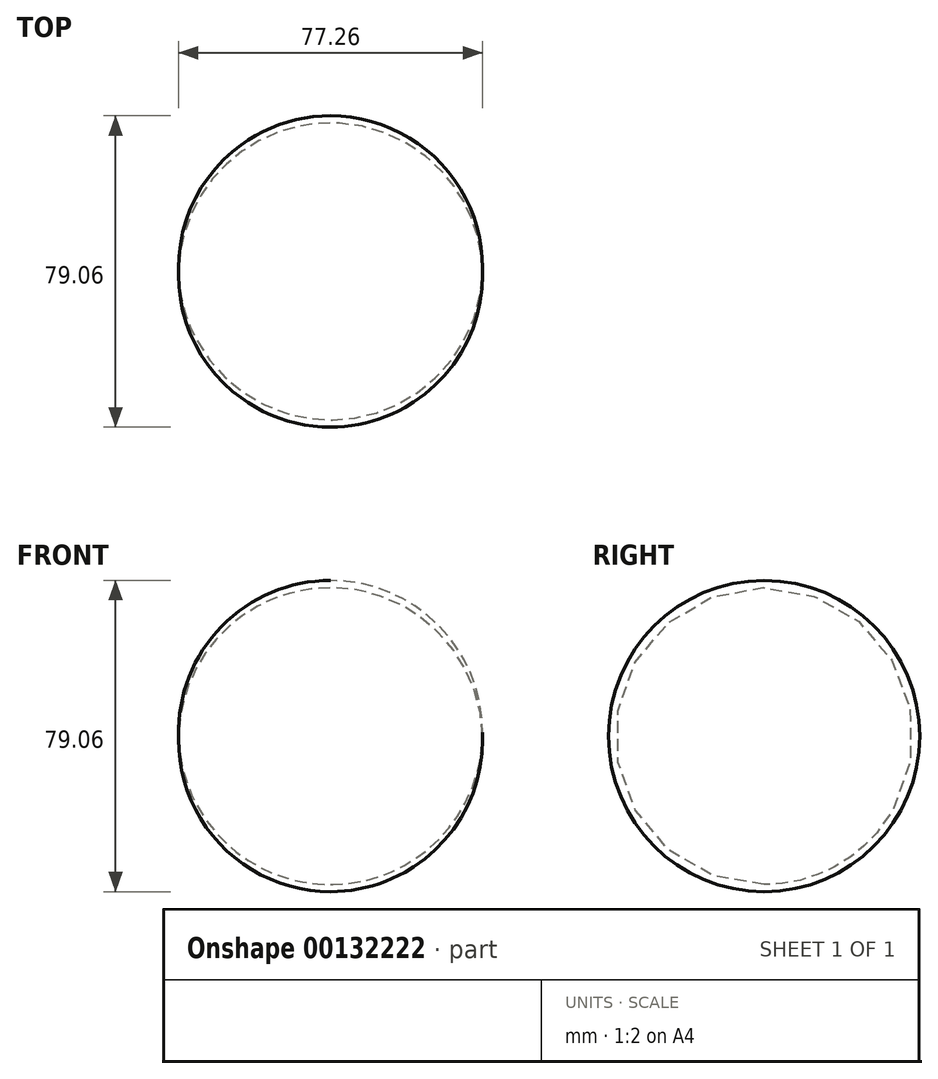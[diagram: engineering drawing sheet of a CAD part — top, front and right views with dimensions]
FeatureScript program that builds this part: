
annotation { "Feature Type Name" : "Feature", "Feature Type Description" : "" }
export const myFeature = defineFeature(function(context is Context, id is Id, definition is map)
    precondition{}
    {
        {
            var Q0;
            Q0=qCreatedBy(makeId("Front.planeOp"),FACE);
            var sketch = newSketch(context, id + "F0", { "sketchPlane" : qUnion([Q0])});
            skArc(sketch, "E0", {"start": v(-40.22, 0) * mm, "mid": v(-1.6, -37.73) * mm, "end": v(37.02, 0) * mm});
            skLineSegment(sketch, "E1", {"start": v(-40.22, 0) * mm, "end": v(47.08, 0) * mm});
            skSolve(sketch);
        }
        {
            var Q0;
            {var subQ0=sQuery(id+"F0.wireOp",EDGE,"E0");Q0=makeQuery(id+"F0.imprint","IMPRINT",FACE,{"disambiguationData":[TD([[makeQuery(id+"F0.imprint","IMPRINT",EDGE,{"derivedFrom":subQ0}),1.0]])]});}
            var Q1;
            Q1=sQuery(id+"F0.wireOp",EDGE,"E1");
            revolve(context, id + "F1", {"entities" : qUnion([Q0]), "axis" : qUnion([Q1]), "revolveType" : RevolveType.FULL});
        }
    });
